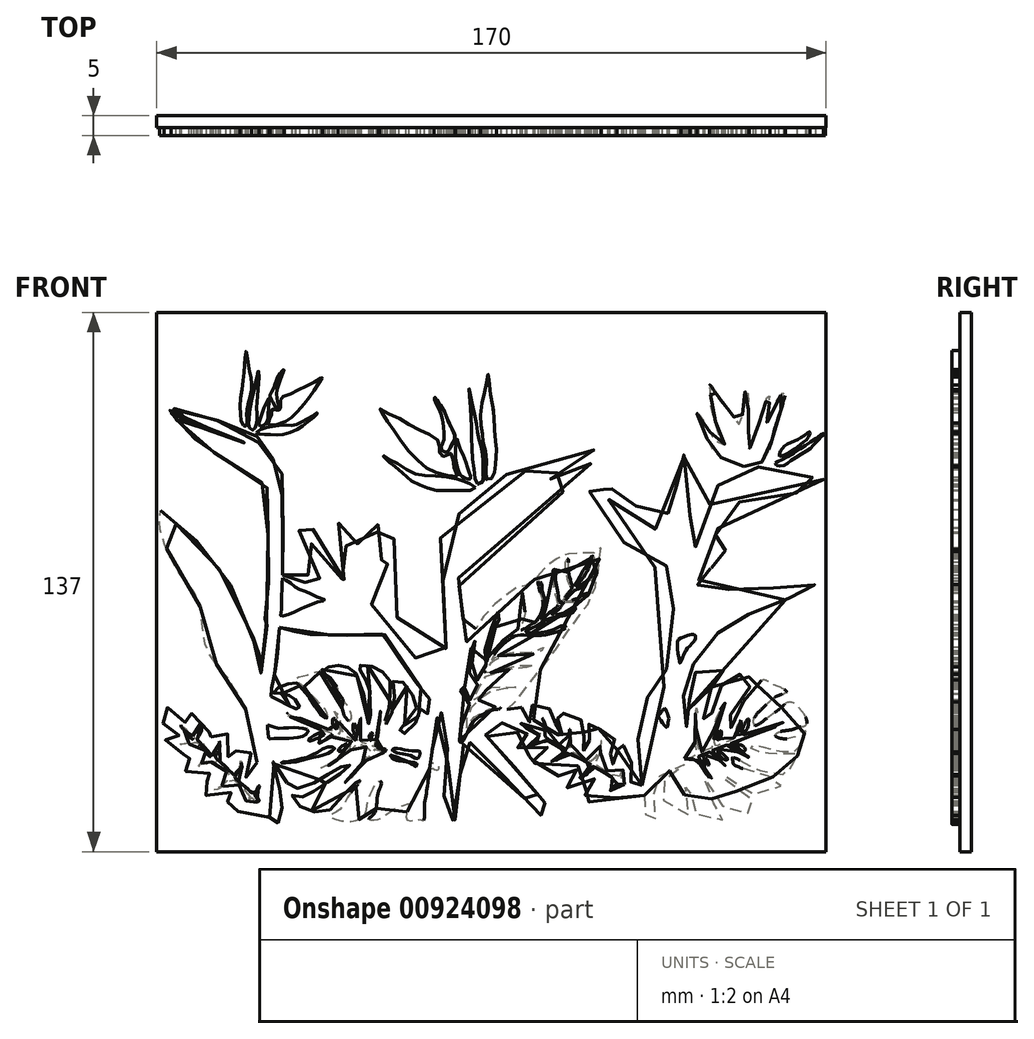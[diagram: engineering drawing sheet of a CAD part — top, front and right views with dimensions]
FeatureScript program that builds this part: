
annotation { "Feature Type Name" : "Feature", "Feature Type Description" : "" }
export const myFeature = defineFeature(function(context is Context, id is Id, definition is map)
    precondition{}
    {
        {
            var Q0;
            Q0=qCreatedBy(makeId("Front.planeOp"),FACE);
            var sketch = newSketch(context, id + "F0", { "sketchPlane" : qUnion([Q0])});
            skLineSegment(sketch, "E0.bottom", {"start": v(0, 0) * mm, "end": v(170, 0) * mm});
            skLineSegment(sketch, "E0.top", {"start": v(0, 137) * mm, "end": v(170, 137) * mm});
            skLineSegment(sketch, "E0.left", {"start": v(0, 0) * mm, "end": v(0, 137) * mm});
            skLineSegment(sketch, "E0.right", {"start": v(170, 0) * mm, "end": v(170, 137) * mm});
            skSolve(sketch);
        }
        {
            var Q0;
            Q0=makeQuery(id+"F0.imprint","IMPRINT",FACE,{"disambiguationData":[TD([[makeQuery(id+"F0.imprint","IMPRINT",EDGE,{"derivedFrom":sQuery(id+"F0.wireOp",EDGE,"E0.bottom")}),1.0]])]});
            extrude(context, id + "F1", {"entities" : qUnion([Q0]), "oppositeDirection" : true, "depth" : 3 * mm, "offsetDistance" : 25 * mm});
        }
        {
            var Q0;
            Q0=makeQuery(id+"F1.opExtrude","CAP_FACE",FACE,{"disambiguationData":[OSD([sQuery(id+"F0.wireOp",EDGE,"E0.bottom"),sQuery(id+"F0.wireOp",EDGE,"E0.top"),sQuery(id+"F0.wireOp",EDGE,"E0.left"),sQuery(id+"F0.wireOp",EDGE,"E0.right")])],"isStart":true});
            var sketch = newSketch(context, id + "F2", { "sketchPlane" : qUnion([Q0])});
            skFitSpline(sketch, "E1", {"points": [v(28.6, 8.72) * mm, v(25.87, 11.7) * mm, v(22.82, 10.25) * mm, v(21.68, 10.12) * mm, v(19.58, 10.31) * mm, v(17.93, 10.7) * mm, v(16.72, 11.26) * mm, v(16.15, 12.15) * mm, v(17.8, 12.66) * mm, v(19.27, 13.04) * mm, v(20.4, 13.74) * mm, v(20.54, 14.38) * mm, v(20.35, 15.27) * mm, v(19.4, 15.52) * mm, v(18.44, 14.57) * mm, v(16.85, 13.49) * mm, v(15.7, 12.98) * mm, v(14.12, 12.92) * mm, v(12.6, 14.25) * mm, v(11.38, 15.71) * mm, v(10.69, 16.35) * mm, v(9.99, 17.18) * mm, v(11.32, 17.68) * mm, v(12.97, 17.94) * mm, v(14.88, 18.7) * mm, v(15.52, 19.53) * mm, v(15.52, 20.42) * mm, v(14.44, 20.42) * mm, v(13.3, 19.9) * mm, v(12.21, 18.83) * mm, v(10.75, 18.38) * mm, v(8.65, 18.64) * mm, v(7.83, 19.72) * mm, v(6.1, 22.26) * mm, v(5.28, 23.34) * mm, v(4.84, 23.78) * mm, v(7.13, 23.91) * mm, v(8.72, 23.6) * mm, v(10.62, 23.6) * mm, v(10.88, 24.42) * mm, v(9.22, 24.87) * mm, v(7.38, 24.74) * mm, v(5.54, 24.61) * mm, v(4.71, 24.61) * mm, v(3.57, 25.82) * mm, v(2.61, 27.15) * mm, v(2.36, 28.1) * mm, v(1.6, 29.89) * mm, v(2.17, 30.14) * mm, v(3.19, 29.76) * mm, v(4.27, 29.5) * mm, v(5.35, 29.19) * mm, v(5.73, 29.82) * mm, v(5.6, 30.27) * mm, v(4.14, 30.52) * mm, v(2.93, 30.58) * mm, v(1.72, 31.28) * mm, v(1.66, 32.43) * mm, v(1.53, 33.76) * mm, v(1.72, 35.1) * mm, v(0.96, 36.62) * mm, v(0.96, 37.32) * mm, v(2.87, 36.56) * mm, v(4.14, 36.37) * mm, v(6.24, 36.11) * mm, v(7, 35.1) * mm, v(7.13, 33.57) * mm, v(7.44, 32.43) * mm, v(8.27, 31.92) * mm, v(8.65, 32.43) * mm, v(8.4, 33.57) * mm, v(8.08, 34.72) * mm, v(8.27, 35.1) * mm, v(9.73, 34.97) * mm, v(11.07, 34.33) * mm, v(12.27, 33.25) * mm, v(13.48, 32.05) * mm, v(13.3, 30.46) * mm, v(12.72, 29.25) * mm, v(12.6, 28.04) * mm, v(12.72, 27.09) * mm, v(13.35, 27.22) * mm, v(13.74, 28.61) * mm, v(13.93, 30.65) * mm, v(14.18, 31.8) * mm, v(15.52, 31.86) * mm, v(17.3, 30.71) * mm, v(18.12, 29.82) * mm, v(18.88, 29.38) * mm, v(19.77, 28.23) * mm, v(19.33, 26.64) * mm, v(18.31, 24.8) * mm, v(18, 23.78) * mm, v(17.49, 22.96) * mm, v(18.06, 22.64) * mm, v(19.14, 22.58) * mm, v(19.71, 24.23) * mm, v(20.1, 25.63) * mm, v(20.35, 26.96) * mm, v(20.47, 28.1) * mm, v(21.93, 27.09) * mm, v(23.4, 25.5) * mm, v(24.35, 24.67) * mm, v(24.8, 23.34) * mm, v(23.9, 21.37) * mm, v(23.02, 20.1) * mm, v(22.63, 19.08) * mm, v(23.14, 18.32) * mm, v(24.73, 18.38) * mm, v(24.99, 19.6) * mm, v(25.43, 21.12) * mm, v(25.43, 22.7) * mm], "startDerivative": vector(-157.55, 285.4) * mm, "endDerivative": vector(-16.17, 168.1) * mm});
            skFitSpline(sketch, "E2", {"points": [v(25.68, 23.09) * mm, v(25.43, 22.7) * mm, v(25.11, 24.61) * mm, v(24.48, 28.74) * mm, v(23.9, 31.67) * mm, v(23.33, 33.95) * mm, v(22.38, 36.81) * mm, v(20.73, 40) * mm, v(18.88, 42.66) * mm, v(17.68, 44.76) * mm, v(15.77, 46.73) * mm, v(15.13, 47.62) * mm, v(14.05, 49) * mm, v(12.34, 52.59) * mm, v(11.8, 56.1) * mm, v(11.18, 61.13) * mm, v(10.19, 64.9) * mm, v(6.41, 69.76) * mm, v(4.34, 72.9) * mm, v(2.82, 76.23) * mm, v(0.84, 81.44) * mm, v(0.75, 85.66) * mm, v(0.75, 86.83) * mm, v(2.64, 84.86) * mm, v(5.7, 82.88) * mm, v(8.12, 81.08) * mm, v(10.64, 78.47) * mm, v(13.33, 75.15) * mm, v(16.12, 71.37) * mm, v(19.35, 66.97) * mm, v(21.96, 61.94) * mm, v(24.12, 56.27) * mm, v(25.1, 50.8) * mm, v(25.65, 47.56) * mm, v(26.19, 44.95) * mm, v(26.28, 44.14) * mm, v(26.63, 46.84) * mm, v(27.17, 50.52) * mm, v(27.53, 54.48) * mm, v(27.9, 57.26) * mm, v(27.9, 57.8) * mm, v(26.72, 58.16) * mm, v(27.77, 58.36) * mm, v(27.8, 58.66) * mm, v(26.75, 58.7) * mm, v(26.37, 58.8) * mm, v(26.4, 59.11) * mm, v(27.4, 59.15) * mm, v(27.92, 59.19) * mm, v(27.92, 60.7) * mm, v(28, 62.1) * mm, v(28, 65.5) * mm, v(28.45, 68.92) * mm, v(28.27, 72.7) * mm, v(28.36, 75.13) * mm, v(28.3, 80.35) * mm, v(28.27, 85.28) * mm, v(28.36, 88.07) * mm, v(28.2, 90.79) * mm, v(28.11, 92.31) * mm, v(26.77, 93.7) * mm, v(24.7, 95.15) * mm, v(21.64, 96.8) * mm, v(19.76, 97.93) * mm, v(18.27, 98.83) * mm, v(13.76, 101.94) * mm, v(11.94, 103.11) * mm, v(9.75, 104.82) * mm, v(7.4, 107.28) * mm, v(6.12, 108.67) * mm, v(5, 109.8) * mm, v(3.71, 110.86) * mm, v(3.66, 111.45) * mm, v(4.46, 110.86) * mm, v(6.86, 109.69) * mm, v(9.38, 108.56) * mm, v(11.46, 107.76) * mm, v(13.22, 106.96) * mm, v(15.68, 106.1) * mm, v(18.67, 104.98) * mm, v(20.92, 104.45) * mm, v(22.79, 103.7) * mm, v(20.22, 105.04) * mm, v(16.96, 106.21) * mm, v(13.65, 107.44) * mm, v(10.28, 108.67) * mm, v(7.99, 109.63) * mm, v(4.3, 111.3) * mm, v(3.55, 111.89) * mm, v(3.08, 112.26) * mm, v(2.41, 112.64) * mm, v(1.8, 113.12) * mm, v(2.52, 113.63) * mm, v(3.7, 112.83) * mm, v(5.38, 112.32) * mm, v(6.53, 111.7) * mm, v(8.1, 111.01) * mm, v(9.81, 110.58) * mm, v(11.95, 110.18) * mm, v(14.7, 109.67) * mm, v(17.38, 109.25) * mm, v(21.25, 108.2) * mm, v(23.3, 107.06) * mm, v(25.15, 105.83) * mm, v(25.87, 104.68) * mm, v(25.95, 103.88) * mm, v(26.97, 103.05) * mm, v(27.74, 102.06) * mm, v(28.84, 100.86) * mm, v(29.5, 99.9) * mm, v(30.44, 98.61) * mm, v(31.36, 96.91) * mm, v(32.08, 94.66) * mm, v(31.9, 92.01) * mm, v(31.86, 89) * mm, v(32, 85.72) * mm, v(32.04, 82.35) * mm, v(31.95, 79.34) * mm, v(31.99, 77.09) * mm, v(31.9, 75) * mm, v(31.92, 73.08) * mm, v(31.92, 71.43) * mm, v(31.95, 70.35) * mm], "startDerivative": vector(-76, -164.8) * mm, "endDerivative": vector(7.76, -185.03) * mm});
            skFitSpline(sketch, "E3", {"points": [v(31.95, 69.57) * mm, v(31.88, 68.2) * mm, v(31.79, 65.88) * mm, v(31.7, 64.1) * mm, v(31.66, 61.08) * mm, v(31.47, 59.81) * mm, v(32.23, 59.94) * mm, v(34.01, 60.51) * mm, v(36.3, 61.6) * mm, v(37.6, 62.1) * mm, v(40.08, 63.12) * mm, v(41.8, 63.66) * mm, v(42.81, 63.98) * mm, v(40.84, 64.7) * mm, v(38.81, 65.66) * mm, v(36.68, 66.52) * mm, v(35.19, 67.25) * mm, v(33.8, 68.36) * mm, v(32.52, 69.19) * mm, v(31.95, 69.57) * mm]});
            skFitSpline(sketch, "E4", {"points": [v(31.15, 56.94) * mm, v(30.96, 54.94) * mm, v(30.84, 53.13) * mm, v(30.73, 51.16) * mm, v(30.54, 49.3) * mm, v(30.24, 47.46) * mm, v(29.94, 45.42) * mm, v(29.6, 43.3) * mm, v(29.22, 41.71) * mm, v(29.14, 40.47) * mm, v(29, 39.45) * mm, v(30.43, 38.73) * mm, v(31.98, 37.93) * mm, v(33.41, 37.18) * mm, v(34.92, 36.54) * mm, v(35.98, 36.08) * mm, v(36.36, 36.42) * mm, v(35.8, 37.44) * mm, v(35.23, 38.46) * mm, v(34.55, 39.33) * mm, v(33.6, 39.75) * mm, v(32.32, 40.09) * mm, v(30.96, 40.16) * mm, v(29.94, 40.16) * mm, v(29.6, 40.54) * mm, v(30.28, 41.26) * mm, v(31.86, 42.17) * mm, v(33.8, 42.7) * mm, v(35.26, 43.04) * mm, v(36.02, 42.4) * mm, v(37.46, 41) * mm, v(38.51, 39.56) * mm, v(39.53, 38) * mm, v(40.7, 36.27) * mm, v(41.58, 34.95) * mm, v(42.03, 34.46) * mm, v(42.97, 34.04) * mm, v(43.43, 33.97) * mm, v(43.35, 35.06) * mm, v(42.67, 36.3) * mm, v(41.58, 37.44) * mm, v(40.78, 38.35) * mm, v(39.38, 39.79) * mm, v(38.44, 40.84) * mm, v(37.3, 41.94) * mm, v(36.62, 42.4) * mm, v(35.76, 43.38) * mm, v(35.3, 43.8) * mm, v(35.9, 44.32) * mm, v(37.34, 44.74) * mm, v(39.04, 45.19) * mm, v(40.37, 45.68) * mm, v(41.5, 45.72) * mm, v(42.48, 44.25) * mm, v(43.7, 43.07) * mm, v(44.79, 41.64) * mm, v(45.54, 40.43) * mm, v(46.1, 39.37) * mm, v(46.53, 38.05) * mm, v(47.13, 36.35) * mm, v(47.62, 34.65) * mm, v(48.38, 33.59) * mm, v(48.87, 33.25) * mm, v(49.4, 33.78) * mm, v(49.44, 34.95) * mm, v(48.83, 36.42) * mm, v(47.85, 37.86) * mm, v(47.05, 39.1) * mm, v(46.56, 40.01) * mm, v(46.1, 41.07) * mm, v(45.4, 42.73) * mm, v(44.45, 43.83) * mm, v(43.2, 44.85) * mm, v(42.33, 45.5) * mm, v(41.8, 46.1) * mm, v(42.67, 46.63) * mm, v(44.33, 47.15) * mm, v(45.5, 47.27) * mm, v(46.68, 47.38) * mm, v(47.77, 47.08) * mm, v(49.17, 46.59) * mm, v(50.12, 46.1) * mm, v(50.83, 44.7) * mm, v(51.4, 43) * mm, v(51.93, 41.98) * mm, v(52.3, 40.8) * mm, v(52.8, 39) * mm, v(52.99, 37.44) * mm, v(53.21, 35.9) * mm, v(53.37, 34.3) * mm, v(53.48, 33.4) * mm, v(53.7, 32.72) * mm, v(53.82, 32.5) * mm, v(54.16, 32.98) * mm, v(54.35, 34.65) * mm, v(54.39, 36.16) * mm, v(54.2, 38.2) * mm, v(54.2, 39.97) * mm, v(53.93, 41.49) * mm, v(53.4, 42.92) * mm, v(52.84, 44.2) * mm, v(51.85, 45.9) * mm, v(51.25, 46.81) * mm, v(51.02, 47.34) * mm, v(51.74, 47.38) * mm, v(53.67, 47.27) * mm, v(55.14, 46.93) * mm, v(56.58, 46.1) * mm, v(57.98, 45.27) * mm, v(59.03, 43.83) * mm, v(59.41, 42.13) * mm, v(59.18, 39.22) * mm, v(59.03, 37.07) * mm, v(58.58, 34.68) * mm, v(57.98, 33.02) * mm, v(58.01, 32.53) * mm, v(58.35, 32.42) * mm, v(58.58, 33.21) * mm, v(59.56, 34.95) * mm, v(60.13, 36.84) * mm, v(60.36, 38.8) * mm, v(60.36, 41.79) * mm, v(60.1, 43.15) * mm, v(59.94, 43.87) * mm, v(61.57, 43.64) * mm, v(63.15, 42.56) * mm, v(64.45, 40.68) * mm, v(65.44, 39.01) * mm, v(65.8, 37.57) * mm, v(65.98, 36.18) * mm, v(64.72, 34.52) * mm, v(63.55, 33.3) * mm, v(62.79, 31.91) * mm, v(61.84, 31.06) * mm, v(61.57, 30.2) * mm, v(61.57, 29.76) * mm, v(62.65, 29.84) * mm, v(63.96, 30.97) * mm, v(65.48, 32.4) * mm, v(66.11, 33.53) * mm, v(66.74, 35.2) * mm, v(67.28, 36.72) * mm, v(68.5, 34.6) * mm, v(68.99, 36.45) * mm, v(69.21, 38.25) * mm, v(69.26, 38.83) * mm, v(66.97, 41.75) * mm, v(63.96, 45.7) * mm, v(59.2, 52.36) * mm, v(58.47, 53.48) * mm, v(58.43, 54.47) * mm, v(58.65, 54.74) * mm, v(57.53, 55.24) * mm, v(55.42, 55.33) * mm, v(52.5, 55.2) * mm, v(50.6, 55.06) * mm, v(47.5, 55.01) * mm, v(44.77, 55.01) * mm, v(41.58, 55.1) * mm, v(39.33, 55.2) * mm, v(36.81, 55.5) * mm, v(34.97, 56) * mm, v(32.59, 56.5) * mm, v(31.15, 56.94) * mm]});
            skFitSpline(sketch, "E5", {"points": [v(28.6, 8.72) * mm, v(29.2, 7.1) * mm, v(31.16, 7.63) * mm, v(31.77, 10.05) * mm, v(31.62, 14.38) * mm, v(30.71, 17.84) * mm, v(30.18, 20.4) * mm, v(29.88, 22.07) * mm, v(29.58, 22.83) * mm, v(30.56, 22.9) * mm, v(30.63, 21.62) * mm, v(31.84, 19.12) * mm, v(33.66, 16.78) * mm, v(34.72, 16.1) * mm, v(37.66, 16.63) * mm, v(40.69, 17.84) * mm, v(43.18, 19.42) * mm, v(45.45, 20.7) * mm, v(47.19, 21.84) * mm, v(48.47, 22.6) * mm, v(49, 21.92) * mm, v(48.32, 21.09) * mm, v(46.13, 19.5) * mm, v(43.94, 18.06) * mm, v(41.3, 16.17) * mm, v(39.33, 15.04) * mm, v(37.9, 14.2) * mm, v(36.3, 13.98) * mm, v(35.1, 14.36) * mm, v(34.34, 14.29) * mm, v(35.32, 12.7) * mm, v(37.2, 11.04) * mm, v(40, 10.2) * mm, v(42.42, 9.83) * mm, v(45.75, 12.32) * mm, v(48.1, 15.2) * mm, v(50.59, 17.61) * mm, v(52.02, 19.05) * mm, v(51.65, 17.84) * mm, v(49.68, 15.5) * mm, v(47.56, 12.17) * mm, v(46.5, 10.8) * mm, v(44.84, 9.68) * mm, v(43.86, 9.07) * mm, v(45.9, 8.09) * mm, v(48.62, 7.71) * mm, v(51.34, 8.16) * mm, v(52.85, 9.3) * mm, v(53.76, 13.38) * mm, v(55.2, 16.55) * mm, v(56.18, 17.99) * mm, v(57.01, 17.69) * mm, v(56.26, 15.2) * mm, v(55.88, 11.87) * mm, v(55.2, 9.6) * mm, v(54.22, 8.77) * mm, v(53.91, 8.24) * mm, v(56.1, 8.24) * mm, v(59.2, 10.13) * mm, v(61.47, 11.41) * mm, v(62.83, 11.8) * mm, v(64.04, 12.17) * mm, v(63.44, 8.24) * mm, v(66.91, 8.16) * mm, v(67.82, 7.94) * mm, v(67.97, 11.04) * mm, v(68.42, 14.59) * mm, v(68.95, 18.14) * mm, v(69.26, 20.48) * mm, v(69.4, 21.16) * mm, v(70.09, 21.16) * mm, v(71.45, 20.86) * mm, v(71.6, 21.84) * mm, v(70.31, 22.45) * mm, v(69.7, 22.67) * mm, v(69.78, 24.8) * mm, v(70.39, 29.48) * mm, v(70.84, 32.8) * mm, v(71.52, 35.52) * mm, v(71.52, 35.98) * mm, v(73.71, 34.01) * mm, v(74.7, 32.65) * mm, v(74.02, 30.61) * mm, v(73.56, 29.4) * mm, v(73.8, 26.3) * mm, v(74.02, 23.43) * mm, v(73.71, 19.88) * mm, v(73.1, 16.33) * mm, v(72.96, 13.23) * mm, v(72.5, 10.66) * mm, v(72.35, 9) * mm, v(72.5, 7.94) * mm, v(73.71, 8.16) * mm, v(75.68, 8.01) * mm, v(75.98, 9.22) * mm, v(76.2, 13.38) * mm, v(76.89, 17.69) * mm, v(77.2, 21.31) * mm, v(77.5, 24.04) * mm, v(77.87, 26.15) * mm, v(77.8, 27.2) * mm, v(79.3, 27.59) * mm, v(80.29, 28.12) * mm, v(81.95, 26.3) * mm, v(85.28, 22.75) * mm, v(88.45, 18.82) * mm, v(92.3, 14.9) * mm, v(94.65, 12.17) * mm, v(97.22, 9.68) * mm, v(98.73, 8.16) * mm, v(100.43, 7.92) * mm, v(102.51, 8.13) * mm, v(99.79, 11.23) * mm, v(96.96, 14.28) * mm, v(95.35, 16.47) * mm, v(92.84, 19.4) * mm, v(90.86, 21.54) * mm, v(89.37, 23.2) * mm, v(87.6, 25.12) * mm, v(84.88, 27.9) * mm, v(83.6, 29.61) * mm, v(82.8, 30.42) * mm, v(84.34, 31.7) * mm, v(86, 33.52) * mm, v(86.96, 34.26) * mm, v(87.5, 33.3) * mm, v(88.14, 31.97) * mm, v(88.78, 30.42) * mm, v(90.06, 30.1) * mm, v(91.67, 30.3) * mm, v(93.54, 30.47) * mm, v(94.07, 29.93) * mm, v(93.16, 29.13) * mm, v(92.04, 29.03) * mm, v(91.3, 29.24) * mm, v(90.33, 29.13) * mm, v(90.7, 28.17) * mm, v(91.61, 26.57) * mm, v(92.95, 25.4) * mm, v(94.5, 24.38) * mm, v(95.89, 24.16) * mm, v(97.01, 25.34) * mm, v(99.15, 26.51) * mm, v(100.22, 26.67) * mm, v(100.75, 25.98) * mm, v(99.36, 24.96) * mm, v(97.5, 24.16) * mm, v(96.16, 23.68) * mm, v(95.73, 22.93) * mm, v(96.42, 22.13) * mm, v(97.44, 21) * mm, v(98.61, 20.05) * mm, v(99.84, 19.57) * mm, v(101.18, 19.09) * mm, v(103.05, 19.89) * mm, v(104.33, 21.38) * mm, v(105.45, 22.45) * mm, v(106.26, 22.99) * mm, v(107, 21.76) * mm, v(106.63, 20.69) * mm, v(105.3, 19.83) * mm, v(103.64, 18.87) * mm, v(101.93, 18.28) * mm, v(102.57, 17.38) * mm, v(104.01, 16.36) * mm, v(105.94, 15.5) * mm, v(108.18, 15.08) * mm, v(109.36, 16.04) * mm, v(110.32, 17.32) * mm, v(110.96, 18.4) * mm, v(112.19, 18.66) * mm, v(113.1, 17.48) * mm, v(112.56, 16.2) * mm, v(110.64, 15.24) * mm, v(109.4, 14.81) * mm, v(108.77, 14.17) * mm, v(109.3, 13) * mm, v(111.01, 12.25) * mm, v(113.95, 12.25) * mm, v(115.66, 13.05) * mm, v(117.59, 14.44) * mm, v(118.81, 15.67) * mm, v(119.56, 16.15) * mm, v(121.43, 15.3) * mm, v(123.25, 14.38) * mm, v(123.84, 14.38) * mm], "startDerivative": vector(40.15, -413.53) * mm, "endDerivative": vector(178.1, 26.6) * mm});
            skFitSpline(sketch, "E6", {"points": [v(123.84, 14.38) * mm, v(123.84, 13.36) * mm, v(123.87, 12.2) * mm, v(123.99, 11.57) * mm, v(124.08, 10.17) * mm, v(124.12, 9.32) * mm, v(124.25, 7.71) * mm, v(124.67, 7.6) * mm, v(125.48, 7.88) * mm, v(126.24, 8.07) * mm, v(126.65, 8.37) * mm, v(126.58, 9.85) * mm, v(126.46, 11.47) * mm, v(126.46, 13.23) * mm, v(126.33, 14.9) * mm, v(126.24, 16.78) * mm, v(126.09, 18.12) * mm, v(126.09, 18.67) * mm, v(127.7, 19.2) * mm, v(129.73, 20.33) * mm, v(132.38, 21.46) * mm, v(134.04, 22.35) * mm, v(133.9, 21.77) * mm, v(132.6, 20.51) * mm, v(130.58, 19.2) * mm, v(129, 18.13) * mm, v(127.8, 16.96) * mm, v(127.2, 16.33) * mm, v(127.8, 14.76) * mm, v(128.96, 12.78) * mm, v(131.07, 11.43) * mm, v(133, 10.27) * mm, v(135.16, 9.37) * mm, v(134.94, 10.36) * mm, v(134.26, 12.56) * mm, v(134.17, 15.7) * mm, v(134.67, 17.32) * mm, v(135.07, 18.13) * mm, v(135.61, 17.6) * mm, v(135.57, 15.88) * mm, v(135.88, 13.9) * mm, v(135.93, 12.38) * mm, v(136.02, 11.03) * mm, v(136.1, 10.27) * mm, v(137.6, 9.37) * mm, v(139.52, 8.47) * mm, v(141.45, 7.93) * mm, v(143.7, 8.1) * mm, v(144.83, 8.24) * mm, v(145.18, 9.05) * mm, v(142.85, 10.8) * mm, v(140.92, 13.5) * mm, v(139.93, 15.48) * mm, v(139.25, 17.46) * mm, v(139.16, 18.49) * mm, v(140.02, 17) * mm, v(141.95, 13.95) * mm, v(143.61, 11.7) * mm, v(145.45, 9.73) * mm, v(147.57, 9.19) * mm, v(149.72, 9.68) * mm, v(152.38, 10.76) * mm, v(153.72, 12.15) * mm, v(152.87, 12.65) * mm, v(150.13, 13.5) * mm, v(146.76, 15.61) * mm, v(144.74, 17.82) * mm, v(143.2, 19.57) * mm, v(142.3, 20.56) * mm, v(142.67, 20.96) * mm, v(143.93, 19.75) * mm, v(145.63, 18.27) * mm, v(148.82, 16.06) * mm, v(151.52, 14.71) * mm, v(154, 13.77) * mm, v(156.55, 14.94) * mm, v(158.71, 16.92) * mm, v(159.61, 18.85) * mm, v(159.52, 19.25) * mm, v(157.36, 19.03) * mm, v(154.44, 19.34) * mm, v(152.55, 20.15) * mm, v(150.76, 20.74) * mm, v(148.78, 21.19) * mm, v(146.44, 22.4) * mm, v(146.3, 23.25) * mm, v(146.26, 23.88) * mm, v(148.38, 23.07) * mm, v(150.94, 21.68) * mm, v(153.68, 20.56) * mm, v(157.1, 19.97) * mm, v(159.84, 19.84) * mm, v(160.91, 21.28) * mm, v(161.9, 22.9) * mm, v(162.71, 24.7) * mm, v(161.45, 25) * mm, v(159.48, 24.78) * mm, v(156.87, 24.87) * mm, v(154.17, 25.14) * mm, v(151.84, 25.77) * mm, v(150.9, 26.3) * mm, v(150.8, 26.76) * mm, v(152.5, 27.07) * mm, v(154.53, 26.49) * mm, v(157.4, 25.73) * mm, v(159.3, 25.5) * mm, v(162.13, 25.46) * mm, v(163.25, 26.67) * mm, v(163.92, 28.15) * mm, v(164.55, 29.95) * mm, v(164.87, 31.07) * mm, v(163.74, 30.67) * mm, v(162.49, 29.45) * mm, v(160.91, 28.7) * mm, v(159.3, 28.7) * mm, v(157.81, 29) * mm, v(157.18, 29.5) * mm, v(157.77, 30.3) * mm, v(161.32, 31.03) * mm, v(163.12, 31.61) * mm, v(164.96, 32.24) * mm, v(164.82, 34.22) * mm, v(163.43, 36.29) * mm, v(162.08, 37.63) * mm, v(160.33, 37.95) * mm, v(158.67, 36.65) * mm, v(156.87, 35.3) * mm, v(154.8, 33.77) * mm, v(153.23, 32.6) * mm, v(151.97, 32.15) * mm, v(151.61, 33.27) * mm, v(152.42, 34.94) * mm, v(154.08, 36.65) * mm, v(155.84, 38.3) * mm, v(157.32, 39.43) * mm, v(159.39, 40.24) * mm, v(159.97, 40.78) * mm, v(157.32, 42.22) * mm, v(155.48, 43.16) * mm, v(154.13, 43.66) * mm, v(153.05, 42.98) * mm, v(151.34, 41.36) * mm, v(150, 39.61) * mm, v(148.65, 37.54) * mm, v(147.3, 34.8) * mm, v(146.4, 32.7) * mm, v(145.68, 31.3) * mm, v(145.18, 30.94) * mm, v(144.56, 31.39) * mm, v(144.42, 32.24) * mm, v(145.36, 34) * mm, v(146.8, 36.78) * mm, v(149.23, 40.02) * mm, v(150.76, 42) * mm, v(152.24, 43.48) * mm, v(151.57, 43.93) * mm, v(148.91, 45) * mm, v(147.48, 45.1) * mm, v(145.68, 45.1) * mm, v(145.05, 44.6) * mm, v(143.93, 43.07) * mm, v(142.94, 40.91) * mm, v(142.22, 38.9) * mm, v(141.54, 36.6) * mm, v(140.38, 33.5) * mm, v(139.7, 31.39) * mm, v(139.16, 31.7) * mm, v(138.9, 33.63) * mm, v(139.57, 36.2) * mm, v(140.24, 39.07) * mm, v(140.83, 41.45) * mm, v(141.5, 42.98) * mm, v(142, 44.33) * mm, v(143.16, 45.54) * mm, v(144.02, 46.17) * mm, v(143.44, 46.79) * mm, v(139.37, 46.6) * mm, v(136.96, 45.58) * mm, v(135.3, 44.37) * mm, v(135.3, 41.26) * mm, v(135.3, 38.78) * mm, v(135.18, 35.03) * mm, v(135.18, 31.91) * mm, v(134.73, 31.53) * mm, v(134.54, 32.49) * mm, v(134.48, 35.92) * mm, v(133.97, 38.46) * mm, v(133.72, 40.88) * mm, v(134.35, 43.54) * mm, v(135.96, 47) * mm, v(139.8, 52.35) * mm, v(142.05, 55.02) * mm, v(142.7, 55.88) * mm, v(143.22, 57.27) * mm, v(147.6, 59.3) * mm, v(154.98, 62.18) * mm, v(159.15, 63.79) * mm, v(163.21, 65.39) * mm, v(166.63, 66.78) * mm, v(167.38, 67.85) * mm, v(165.56, 67.2) * mm, v(160.54, 67.1) * mm, v(154.23, 66.89) * mm, v(148.68, 66.57) * mm, v(143.44, 66.57) * mm, v(139.06, 66.67) * mm, v(137.67, 67.53) * mm, v(137.37, 67.88) * mm, v(137.45, 68.57) * mm, v(138.13, 69.57) * mm, v(139.21, 70.47) * mm, v(140.6, 71.9) * mm, v(141.12, 72.29) * mm, v(141.87, 72.9) * mm, v(142.36, 73.37) * mm, v(142.76, 73.59) * mm, v(143.14, 73.94) * mm, v(143.57, 74.43) * mm, v(143.82, 74.72) * mm, v(143.93, 75.16) * mm, v(144.04, 75.6) * mm, v(144.04, 75.86) * mm, v(144.31, 76.1) * mm, v(144.42, 76.65) * mm, v(144.12, 76.6) * mm, v(143.45, 76.26) * mm, v(143.07, 76.51) * mm, v(142.61, 76.7) * mm, v(141.75, 76.86) * mm, v(140.88, 76.83) * mm, v(140.88, 77.88) * mm, v(141.3, 78.93) * mm, v(142.02, 80.86) * mm, v(142.82, 82.8) * mm, v(143.68, 84.36) * mm, v(144.38, 86.2) * mm, v(145.27, 87.76) * mm, v(146.22, 88.55) * mm, v(148.67, 88.87) * mm, v(151.34, 89.16) * mm, v(154.32, 89.54) * mm, v(158.4, 90.11) * mm, v(161.82, 90.94) * mm, v(164.62, 91.86) * mm, v(166.81, 92.56) * mm, v(169.26, 93.7) * mm, v(169.83, 94.47) * mm, v(168.75, 94.69) * mm, v(166.62, 95.07) * mm, v(163.47, 95.77) * mm, v(160.93, 96.3) * mm, v(157.82, 97.3) * mm, v(155.56, 97.67) * mm, v(151.86, 97.71) * mm, v(149.86, 97.33) * mm, v(148.68, 96.88) * mm, v(147.13, 95.94) * mm, v(145.47, 95.07) * mm, v(143.17, 93.56) * mm, v(142, 92.27) * mm, v(140.82, 88.95) * mm, v(138.74, 83.97) * mm, v(137.4, 79.27) * mm, v(136.33, 75.58) * mm, v(135.53, 73.6) * mm, v(135.2, 74.57) * mm, v(135.14, 81.45) * mm, v(135.4, 85.52) * mm, v(135.07, 89.52) * mm, v(134.63, 93.97) * mm, v(134.44, 96.83) * mm, v(134, 99.95) * mm, v(133.61, 102.49) * mm, v(133.17, 101.4) * mm, v(133.36, 98.04) * mm, v(132.85, 95.12) * mm, v(132.21, 92.83) * mm, v(132.09, 94.42) * mm, v(131.13, 97.09) * mm, v(130.62, 94.99) * mm, v(130.37, 91.56) * mm, v(129.86, 86.35) * mm, v(129.48, 82.91) * mm, v(128.72, 81) * mm, v(126.75, 81.9) * mm, v(123.57, 85.96) * mm, v(119.95, 89.78) * mm, v(117.09, 93.2) * mm, v(117.21, 91.56) * mm, v(118.23, 89.52) * mm, v(116.2, 91.62) * mm, v(113.72, 94.6) * mm, v(112.32, 97.09) * mm, v(111.05, 98.04) * mm, v(112.32, 94.86) * mm, v(113.72, 91.62) * mm, v(114.86, 89.27) * mm, v(112.83, 91.5) * mm, v(110.92, 92.7) * mm, v(109.4, 94.29) * mm, v(110.35, 90.48) * mm, v(111.56, 88.38) * mm, v(114.74, 84.25) * mm, v(116.39, 81.32) * mm, v(118.61, 78.66) * mm, v(120.4, 76.05) * mm, v(122.62, 73.25) * mm, v(124.33, 72.36) * mm, v(127.38, 72.36) * mm, v(129.67, 72.55) * mm, v(130.18, 70.84) * mm, v(131, 68.93) * mm, v(131.77, 67.02) * mm, v(132.68, 65.06) * mm, v(131.54, 62.34) * mm, v(130.71, 60.14) * mm, v(128.82, 57.05) * mm, v(128.6, 52.36) * mm, v(129.28, 47.9) * mm, v(129.65, 44.5) * mm, v(129.58, 42.76) * mm, v(127.84, 40.65) * mm, v(126.25, 38.3) * mm, v(125.5, 37.77) * mm, v(124.74, 39.06) * mm, v(123.84, 40.12) * mm, v(123.76, 38.9) * mm, v(123.38, 35.8) * mm, v(123.15, 32.18) * mm, v(122.25, 29.3) * mm, v(122.55, 27.2) * mm, v(122.85, 25.08) * mm, v(122.78, 22.28) * mm, v(123, 19.48) * mm, v(123.08, 18.05) * mm, v(123.23, 16.84) * mm], "startDerivative": vector(0.15, -464.66) * mm, "endDerivative": vector(79.05, -529.4) * mm});
            skFitSpline(sketch, "E7", {"points": [v(123.23, 16.84) * mm, v(122.45, 16.84) * mm, v(121.47, 17.14) * mm, v(120.89, 17.46) * mm, v(120.43, 17.72) * mm, v(120.6, 18.63) * mm, v(120.98, 21.48) * mm, v(120.26, 23.3) * mm, v(119.6, 25.02) * mm, v(118.62, 26.98) * mm, v(117.64, 27.74) * mm, v(117.15, 27.81) * mm, v(117.07, 26.68) * mm, v(117.13, 25.45) * mm, v(117, 23.6) * mm, v(116.31, 22.58) * mm, v(115.44, 22.22) * mm, v(114.69, 22.71) * mm, v(114.69, 23.6) * mm, v(115.31, 24.98) * mm, v(115.9, 26.26) * mm, v(116.3, 27.64) * mm, v(116.33, 28.59) * mm, v(115.37, 29.38) * mm, v(113.74, 30.46) * mm, v(112.72, 31) * mm, v(111.93, 31.57) * mm, v(111.02, 32.1) * mm, v(109.93, 32.54) * mm, v(109.68, 31.76) * mm, v(109.81, 30.36) * mm, v(109.87, 28.8) * mm, v(109.8, 27.4) * mm, v(109.34, 26.4) * mm, v(108.95, 25.77) * mm, v(108.38, 25.77) * mm, v(107.85, 26.3) * mm, v(107.72, 27.3) * mm, v(108.47, 28.98) * mm, v(108.87, 30.33) * mm, v(109.08, 31.65) * mm, v(107.55, 33.67) * mm, v(106.22, 34.01) * mm, v(103.8, 35.05) * mm, v(102.62, 35.43) * mm, v(101.58, 35.75) * mm, v(101.52, 34.75) * mm, v(102.07, 33.25) * mm, v(102.7, 31.74) * mm, v(102.92, 30.17) * mm, v(102.94, 29.51) * mm, v(102.2, 29.59) * mm, v(101.58, 31.06) * mm, v(101.22, 33.75) * mm, v(101.03, 35.14) * mm, v(100.31, 36.1) * mm, v(98.76, 36.58) * mm, v(96.7, 37.1) * mm, v(95.74, 37.24) * mm, v(94.4, 37.35) * mm, v(93.85, 37.01) * mm, v(94.45, 35.98) * mm, v(95.5, 34.5) * mm, v(95.72, 33.5) * mm, v(95.51, 32.8) * mm, v(94.66, 33) * mm, v(94.07, 34.31) * mm, v(93.3, 36.01) * mm, v(92.32, 36.8) * mm, v(90.79, 36.7) * mm, v(89.4, 36.18) * mm, v(88.95, 36.15) * mm, v(90.22, 37.17) * mm, v(94.14, 42.1) * mm, v(99.28, 48.62) * mm, v(102.9, 53.65) * mm, v(107.24, 59.99) * mm, v(109.15, 62.3) * mm, v(111.44, 67.47) * mm, v(112.07, 70.69) * mm, v(112.45, 74.37) * mm, v(112.65, 76.17) * mm, v(112.8, 77.31) * mm, v(111.66, 76.17) * mm, v(109.82, 75.76) * mm, v(107.01, 75.97) * mm, v(103.98, 75.52) * mm, v(101.42, 74.4) * mm, v(98.47, 72.01) * mm, v(96.43, 69.67) * mm, v(94.65, 68.03) * mm, v(93.01, 67.34) * mm, v(91.2, 66.93) * mm, v(89.37, 65.63) * mm, v(86.88, 63.79) * mm, v(83.76, 60.69) * mm, v(81.49, 57.36) * mm, v(80.16, 55.27) * mm, v(78.32, 52.75) * mm, v(77.37, 51.18) * mm, v(77.33, 53.2) * mm, v(77.46, 57.85) * mm, v(77.85, 59.42) * mm, v(78.53, 61.82) * mm, v(79.18, 63.64) * mm, v(78.23, 63.86) * mm, v(77.08, 63.96) * mm, v(76.55, 64.28) * mm, v(76.74, 67.47) * mm, v(76.87, 72.6) * mm, v(79.92, 75.5) * mm, v(85.64, 79.05) * mm, v(94.79, 84.93) * mm, v(100.45, 89.15) * mm, v(105.28, 93.41) * mm, v(109.06, 97.42) * mm, v(111.76, 100.12) * mm, v(110.58, 99.39) * mm, v(107.28, 97.7) * mm, v(103.2, 95.92) * mm, v(100.06, 94.46) * mm, v(101.05, 95.86) * mm, v(106.3, 98.15) * mm, v(110.68, 100.25) * mm, v(112.84, 101.8) * mm, v(112.23, 102.4) * mm, v(106.2, 99.39) * mm, v(99.9, 97.7) * mm, v(92.4, 96.5) * mm, v(87.16, 95.38) * mm, v(82.8, 93.2) * mm, v(80.33, 91.32) * mm, v(79.66, 89.44) * mm, v(78.55, 87.82) * mm, v(74.58, 83.34) * mm, v(72.23, 80.07) * mm, v(70.96, 76.03) * mm, v(70.9, 73.36) * mm, v(73.52, 66.77) * mm, v(73.58, 63.21) * mm, v(74.03, 58.44) * mm, v(74.28, 54.85) * mm, v(73.7, 52.4) * mm, v(72.44, 48.45) * mm, v(71.28, 44.45) * mm, v(70.78, 42.7) * mm, v(68.17, 45.8) * mm, v(64.53, 50.84) * mm, v(62.92, 53.9) * mm, v(62.2, 57.98) * mm, v(57.88, 61.67) * mm, v(53.61, 63.06) * mm, v(50.74, 64.1) * mm, v(50.33, 65.17) * mm, v(53.61, 66.92) * mm, v(57.2, 70.52) * mm, v(59.73, 76.72) * mm, v(60.62, 81.26) * mm, v(60.17, 79.96) * mm, v(58.92, 77.93) * mm, v(58.02, 75.55) * mm, v(55.77, 72.63) * mm, v(53.93, 71.15) * mm, v(54.6, 72.54) * mm, v(56.04, 76.94) * mm, v(56.12, 82.11) * mm, v(56.31, 85.06) * mm, v(56.23, 86.99) * mm, v(55.18, 85.6) * mm, v(53.48, 82.83) * mm, v(51.89, 79.96) * mm, v(50.8, 77.96) * mm, v(49.85, 76.4) * mm, v(49.58, 75.54) * mm, v(48.53, 76.67) * mm, v(47.5, 80) * mm, v(46.4, 84.42) * mm, v(46.18, 83.51) * mm, v(46.07, 80.15) * mm, v(46.52, 76.37) * mm, v(47.05, 74.78) * mm, v(47.05, 73.88) * mm, v(47.35, 70.85) * mm, v(47.47, 68.78) * mm, v(45.54, 72.18) * mm, v(43.16, 76.4) * mm, v(40.82, 81.06) * mm, v(39.72, 82.34) * mm, v(39.99, 81.1) * mm, v(40.9, 78.64) * mm, v(42.18, 75.16) * mm, v(42.1, 74.9) * mm, v(38.44, 79.28) * mm, v(35.98, 81.85) * mm, v(35.45, 82.23) * mm, v(36.06, 80.26) * mm, v(37.68, 76.9) * mm, v(39.34, 73.35) * mm, v(40.7, 70.32) * mm, v(41.84, 68.78) * mm, v(40.33, 69.34) * mm, v(37.68, 70.55) * mm, v(35.45, 70.93) * mm, v(34.47, 71.2) * mm, v(36.02, 69.5) * mm, v(39.5, 67.72) * mm, v(41.8, 66.81) * mm, v(41.53, 66.55) * mm, v(37.6, 68.06) * mm, v(34.66, 69.34) * mm, v(31.95, 70.35) * mm], "startDerivative": vector(-273.48, -21.12) * mm, "endDerivative": vector(-531.95, 194.07) * mm});
            skArc(sketch, "E8", {"start": v(9.72, 28.63) * mm, "mid": v(10.86, 30.48) * mm, "end": v(10.8, 32.65) * mm});
            skSolve(sketch);
        }
        {
            var Q0;
            Q0 = qSketchRegion(id + "F2", true);
            extrude(context, id + "F3", {"entities" : qUnion([Q0]), "operationType" : NewBodyOperationType.ADD, "depth" : 2 * mm, "offsetDistance" : 25 * mm});
        }
        {
            var Q0;
            {var subQ0=sQuery(id+"F0.wireOp",EDGE,"E0.left");var subQ1=sQuery(id+"F0.wireOp",EDGE,"E0.top");var subQ2=sQuery(id+"F0.wireOp",EDGE,"E0.right");var subQ3=sQuery(id+"F0.wireOp",EDGE,"E0.bottom");Q0=makeQuery(id+"F3.boolean.opBoolean","SPLIT",FACE,{"disambiguationData":[TD([makeQuery(id+"F1.opExtrude","SWEPT_FACE",FACE,{"disambiguationData":[OSD([subQ3])]})])],"derivedFrom":makeQuery(id+"F1.opExtrude","CAP_FACE",FACE,{"disambiguationData":[OSD([subQ3,subQ1,subQ0,subQ2])],"isStart":true})});}
            var sketch = newSketch(context, id + "F4", { "sketchPlane" : qUnion([Q0])});
            skFitSpline(sketch, "E9", {"points": [v(22.05, 108.28) * mm, v(21.36, 110.1) * mm, v(21.16, 113.37) * mm, v(21.73, 118.05) * mm, v(22.17, 122.24) * mm, v(22.46, 125.66) * mm, v(22.7, 127.3) * mm, v(22.82, 126.89) * mm, v(23.2, 124.48) * mm, v(23.6, 121.96) * mm, v(24.09, 119.68) * mm, v(24, 117.03) * mm, v(23.35, 114.22) * mm, v(22.87, 110.76) * mm, v(22.95, 108.44) * mm, v(22.05, 108.28) * mm]});
            skFitSpline(sketch, "E10", {"points": [v(24.37, 107.1) * mm, v(23.48, 107.91) * mm, v(23.44, 109.46) * mm, v(23.72, 112.55) * mm, v(24.2, 115.36) * mm, v(24.94, 118.5) * mm, v(25.47, 120.9) * mm, v(25.8, 122.33) * mm, v(25.92, 120.41) * mm, v(25.76, 117.36) * mm, v(25.43, 114.18) * mm, v(25.43, 111.66) * mm, v(25.43, 109.42) * mm, v(24.98, 107.75) * mm, v(24.37, 107.1) * mm]});
            skFitSpline(sketch, "E11", {"points": [v(25.92, 108.44) * mm, v(26.4, 110.4) * mm, v(27.1, 112.51) * mm, v(28.12, 114.63) * mm, v(28.36, 115.12) * mm, v(28.53, 113.82) * mm, v(28.28, 111.5) * mm, v(28.32, 110.64) * mm, v(27.63, 108.77) * mm, v(26.49, 108.2) * mm, v(25.92, 108.44) * mm]});
            skFitSpline(sketch, "E12", {"points": [v(30.36, 112.84) * mm, v(29.58, 114.1) * mm, v(29.1, 114.91) * mm, v(28.73, 115.93) * mm, v(29.5, 117.44) * mm, v(30.6, 120.2) * mm, v(32.23, 122.53) * mm, v(32.07, 121.63) * mm, v(31.1, 119.1) * mm, v(30.44, 116.22) * mm, v(30.8, 114.14) * mm, v(30.97, 113.08) * mm, v(30.36, 112.84) * mm]});
            skFitSpline(sketch, "E13", {"points": [v(28.28, 108.44) * mm, v(32.35, 109.1) * mm, v(34.84, 110.92) * mm, v(37.93, 114.34) * mm, v(39.97, 117.32) * mm, v(41.76, 119.92) * mm, v(42.13, 120.66) * mm, v(40.99, 119.8) * mm, v(37.24, 118) * mm, v(33.74, 116.22) * mm, v(31.54, 115.2) * mm, v(31.5, 114.14) * mm, v(31.38, 112.84) * mm, v(31.13, 112.27) * mm, v(30.32, 112.27) * mm, v(29.3, 112.39) * mm, v(29.18, 111.53) * mm, v(28.9, 110.52) * mm, v(28.28, 108.44) * mm]});
            skFitSpline(sketch, "E14", {"points": [v(25.29, 106.55) * mm, v(27.13, 107.54) * mm, v(29.23, 108.03) * mm, v(32.5, 108.46) * mm, v(34.56, 108.34) * mm, v(36.3, 109) * mm, v(38.5, 110.08) * mm, v(40.5, 111.37) * mm, v(40.8, 111.6) * mm, v(40.66, 111.1) * mm, v(38.55, 109.38) * mm, v(36.2, 107.59) * mm, v(32.98, 106.2) * mm, v(30.18, 105.94) * mm, v(27.73, 106.06) * mm, v(25.77, 106.2) * mm, v(25.29, 106.55) * mm]});
            skFitSpline(sketch, "E15", {"points": [v(80.94, 92.56) * mm, v(79.77, 91.89) * mm, v(74.93, 91.89) * mm, v(70.62, 91.84) * mm, v(67.77, 92.9) * mm, v(65.15, 93.92) * mm, v(61.28, 97.26) * mm, v(59.63, 98.52) * mm, v(58.08, 99.92) * mm, v(57.35, 100.9) * mm, v(58.56, 99.97) * mm, v(60.55, 98.96) * mm, v(64.13, 96.68) * mm, v(67.43, 95.61) * mm, v(71.78, 95.42) * mm, v(76.05, 94.7) * mm, v(77.7, 94.21) * mm, v(79.24, 93.58) * mm, v(80.94, 92.56) * mm]});
            skFitSpline(sketch, "E16", {"points": [v(76.43, 95.34) * mm, v(73.28, 95.77) * mm, v(69.85, 96.7) * mm, v(67.13, 98.68) * mm, v(63.89, 101.83) * mm, v(61.03, 105.9) * mm, v(58.9, 108.94) * mm, v(57.45, 111.12) * mm, v(56.58, 112.58) * mm, v(58.08, 111.6) * mm, v(61.61, 110.15) * mm, v(64.52, 108.31) * mm, v(68.15, 106.57) * mm, v(70.81, 105.07) * mm, v(71.88, 103.81) * mm, v(71.69, 102.5) * mm, v(71.88, 101.34) * mm, v(72.22, 100.47) * mm, v(74.1, 100.95) * mm, v(74.88, 101.15) * mm, v(75.27, 99.7) * mm, v(75.42, 97.85) * mm, v(76.43, 95.34) * mm]});
            skFitSpline(sketch, "E17", {"points": [v(77.06, 95.82) * mm, v(78.03, 95.05) * mm, v(79.63, 94.7) * mm, v(79.24, 96.74) * mm, v(77.98, 100.37) * mm, v(76.87, 102.94) * mm, v(76.19, 104.92) * mm, v(75.95, 102.5) * mm, v(75.95, 99.4) * mm, v(77.06, 95.82) * mm]});
            skFitSpline(sketch, "E18", {"points": [v(73.48, 101.44) * mm, v(74.88, 103.28) * mm, v(75.8, 105.22) * mm, v(74.45, 108.46) * mm, v(73.24, 111.46) * mm, v(71.44, 114.42) * mm, v(70.52, 115.48) * mm, v(70.81, 114.03) * mm, v(71.93, 111.9) * mm, v(72.7, 109) * mm, v(73, 105.07) * mm, v(72.46, 103.42) * mm, v(72.17, 102.3) * mm, v(73.48, 101.44) * mm]});
            skFitSpline(sketch, "E19", {"points": [v(81.48, 93.5) * mm, v(80.68, 95.97) * mm, v(80.1, 101.62) * mm, v(79.99, 108.01) * mm, v(79.64, 113.2) * mm, v(79.35, 117.68) * mm, v(79.93, 114.92) * mm, v(81.2, 108.82) * mm, v(81.71, 105.3) * mm, v(82.46, 102.6) * mm, v(82.87, 99.2) * mm, v(82.87, 95.92) * mm, v(82.92, 94.3) * mm, v(81.48, 93.5) * mm]});
            skFitSpline(sketch, "E20", {"points": [v(83.73, 94.65) * mm, v(83.73, 97.64) * mm, v(83.62, 101.39) * mm, v(82.87, 104.38) * mm, v(82.64, 106.8) * mm, v(82.23, 110.37) * mm, v(82.93, 115.68) * mm, v(83.8, 119.07) * mm, v(84.2, 121.4) * mm, v(84.68, 116.75) * mm, v(85.55, 112.1) * mm, v(85.84, 105.8) * mm, v(86.29, 102.63) * mm, v(86.2, 100.48) * mm, v(86, 98.28) * mm, v(85.64, 95.75) * mm, v(84.82, 94.61) * mm, v(83.73, 94.65) * mm]});
            skFitSpline(sketch, "E21", {"points": [v(149.13, 97.94) * mm, v(145.91, 98.97) * mm, v(143.17, 100.27) * mm, v(141.26, 102.39) * mm, v(139.68, 105.06) * mm, v(138.58, 108.07) * mm, v(137.28, 111.57) * mm, v(139.13, 109.1) * mm, v(140.91, 106.02) * mm, v(142.49, 104.17) * mm, v(144.2, 103.55) * mm, v(143.1, 105.6) * mm, v(141.94, 109.1) * mm, v(140.78, 113.48) * mm, v(140.64, 116.98) * mm, v(140.5, 118.62) * mm, v(141.53, 117.25) * mm, v(144.2, 113.55) * mm, v(146.94, 109.92) * mm, v(147.7, 108.55) * mm, v(148.58, 110.06) * mm, v(149.06, 113) * mm, v(149.34, 115.81) * mm, v(149.68, 117.39) * mm, v(150.43, 114.85) * mm, v(150.16, 110.95) * mm, v(150.36, 108.14) * mm, v(150.36, 106.36) * mm, v(150.36, 103.62) * mm, v(150.5, 102.32) * mm, v(151.46, 104.65) * mm, v(152.7, 108.21) * mm, v(153.92, 111.7) * mm, v(154.6, 113.96) * mm, v(154.95, 115.4) * mm, v(155.36, 116.43) * mm, v(155.7, 114.1) * mm, v(154.81, 111.09) * mm, v(154.81, 108.96) * mm, v(156.8, 113.35) * mm, v(159, 116.43) * mm, v(159.68, 117.04) * mm, v(158.38, 111.7) * mm, v(156.66, 106.36) * mm, v(155.64, 102.6) * mm, v(154.2, 99.65) * mm, v(153.3, 98.62) * mm, v(151.46, 98.55) * mm, v(149.13, 97.94) * mm]});
            skFitSpline(sketch, "E22", {"points": [v(158.2, 100.44) * mm, v(158.44, 101.7) * mm, v(159.75, 103.3) * mm, v(162.12, 104.42) * mm, v(164.4, 105.72) * mm, v(165.9, 106.7) * mm, v(165.46, 105.2) * mm, v(163.58, 103.54) * mm, v(161.25, 101.8) * mm, v(158.2, 100.44) * mm]});
            skFitSpline(sketch, "E23", {"points": [v(157.23, 98.8) * mm, v(157.62, 98.07) * mm, v(159.31, 98.22) * mm, v(161.35, 99.52) * mm, v(165.27, 101.95) * mm, v(167.26, 103.69) * mm, v(169.34, 106.3) * mm, v(167.5, 105.1) * mm, v(163.24, 102.24) * mm, v(158.64, 99.52) * mm, v(157.23, 98.8) * mm]});
            skSolve(sketch);
        }
        {
            var Q0;
            Q0 = qSketchRegion(id + "F4", true);
            extrude(context, id + "F5", {"entities" : qUnion([Q0]), "operationType" : NewBodyOperationType.ADD, "depth" : 2 * mm, "offsetDistance" : 25 * mm});
        }
        {
            var Q0;
            Q0=makeQuery(id+"F3.opExtrude","CAP_FACE",FACE,{"disambiguationData":[OSD([sQuery(id+"F2.wireOp",EDGE,"E1"),sQuery(id+"F2.wireOp",EDGE,"E2"),sQuery(id+"F2.wireOp",EDGE,"E3"),sQuery(id+"F2.wireOp",EDGE,"E4"),sQuery(id+"F2.wireOp",EDGE,"E5"),sQuery(id+"F2.wireOp",EDGE,"E6"),sQuery(id+"F2.wireOp",EDGE,"E7")])],"isStart":false});
            var sketch = newSketch(context, id + "F6", { "sketchPlane" : qUnion([Q0])});
            skFitSpline(sketch, "E24", {"points": [v(25.46, 12.51) * mm, v(24.3, 13.66) * mm, v(23.64, 13.18) * mm, v(22.98, 12.82) * mm, v(22.43, 12.82) * mm, v(23.46, 13.48) * mm, v(23.7, 14.2) * mm, v(21.89, 16.02) * mm, v(20.62, 17.35) * mm, v(19.43, 18.31) * mm, v(18.56, 17.96) * mm, v(17.3, 16.87) * mm, v(15.72, 15.96) * mm, v(14.27, 15.6) * mm, v(15.96, 16.39) * mm, v(17.6, 17.66) * mm, v(18.56, 18.87) * mm, v(18.62, 19.53) * mm, v(17.84, 20.38) * mm, v(16.38, 21.47) * mm, v(15.3, 22.68) * mm, v(14.58, 23.06) * mm, v(13.12, 22.5) * mm, v(11.85, 22.07) * mm, v(10.4, 21.65) * mm, v(10.94, 22.17) * mm, v(13.12, 23.22) * mm, v(13.96, 23.77) * mm, v(13.06, 24.55) * mm, v(12.21, 26) * mm, v(10.94, 27.15) * mm, v(10.1, 27.7) * mm, v(8.76, 27.4) * mm, v(7.61, 27.15) * mm, v(5.86, 27.27) * mm, v(6.64, 27.46) * mm, v(8.34, 27.82) * mm, v(9.37, 28.24) * mm, v(8.22, 29.27) * mm, v(7.25, 30.6) * mm, v(6.28, 31.63) * mm, v(6.16, 32.17) * mm, v(7.85, 30.6) * mm, v(9.25, 29.27) * mm, v(9.88, 28.77) * mm, v(10.64, 30.06) * mm, v(11, 31.5) * mm, v(11.06, 32.78) * mm, v(11.36, 30.84) * mm, v(10.58, 29.27) * mm, v(10.43, 28.3) * mm, v(11.9, 27.21) * mm, v(12.82, 25.88) * mm, v(13.96, 24.55) * mm, v(14.7, 24.8) * mm, v(15.23, 26.25) * mm, v(15.78, 28.18) * mm, v(16.02, 26.8) * mm, v(15.42, 25.04) * mm, v(14.93, 24.07) * mm, v(16.02, 22.86) * mm, v(17.41, 21.77) * mm, v(18.44, 20.56) * mm, v(19.47, 19.4) * mm, v(20.07, 20.32) * mm, v(21.22, 22.2) * mm, v(21.28, 23.1) * mm, v(21.59, 21.16) * mm, v(20.2, 19.65) * mm, v(19.86, 18.77) * mm, v(20.47, 18.14) * mm, v(21.08, 17.63) * mm, v(21.84, 17.07) * mm, v(22.86, 16.28) * mm, v(23.8, 15.24) * mm, v(24.74, 14.98) * mm, v(25.43, 15.77) * mm, v(26, 16.97) * mm, v(26.04, 16.38) * mm, v(25.25, 14.9) * mm, v(24.9, 14.4) * mm, v(25.48, 13.69) * mm, v(26.07, 13.15) * mm, v(25.46, 12.51) * mm]});
            skFitSpline(sketch, "E25", {"points": [v(28.15, 32.21) * mm, v(28.3, 30.33) * mm, v(28.5, 28.7) * mm, v(30.13, 28.8) * mm, v(32.88, 28.75) * mm, v(35.58, 29.06) * mm, v(37.76, 29.62) * mm, v(38.48, 30.74) * mm, v(37.3, 31.35) * mm, v(34.97, 31.55) * mm, v(31.86, 31.4) * mm, v(29.73, 31.65) * mm, v(28.15, 32.21) * mm]});
            skFitSpline(sketch, "E26", {"points": [v(41.88, 30.4) * mm, v(40.66, 29.98) * mm, v(39.56, 29.3) * mm, v(38.67, 28.67) * mm, v(38.63, 28.23) * mm, v(39.4, 28.31) * mm, v(40.29, 28.62) * mm, v(41.23, 29.02) * mm, v(41.98, 29.4) * mm, v(42.45, 29.7) * mm, v(42.53, 29.99) * mm, v(42.2, 30.22) * mm, v(41.88, 30.4) * mm]});
            skFitSpline(sketch, "E27", {"points": [v(32.25, 22.93) * mm, v(31.67, 22.6) * mm, v(33.25, 22.69) * mm, v(35.54, 22.9) * mm, v(38.2, 23.62) * mm, v(40.99, 24.2) * mm, v(42.99, 24.83) * mm, v(44.62, 25.65) * mm, v(45.16, 26.35) * mm, v(44.38, 26.7) * mm, v(42.23, 26.1) * mm, v(39.48, 24.56) * mm, v(37.12, 23.74) * mm, v(34.67, 23.17) * mm, v(32.76, 22.87) * mm, v(32.25, 22.93) * mm]});
            skFitSpline(sketch, "E28", {"points": [v(48.3, 27.4) * mm, v(46.96, 26.76) * mm, v(46.27, 26.1) * mm, v(46.14, 25.56) * mm, v(46.7, 25.51) * mm, v(47.97, 26.38) * mm, v(48.28, 26.84) * mm, v(48.3, 27.4) * mm]});
            skFitSpline(sketch, "E29", {"points": [v(65.84, 21.66) * mm, v(66.05, 22.32) * mm, v(64.47, 22.77) * mm, v(61.78, 23.74) * mm, v(60, 24.4) * mm, v(59.33, 24.5) * mm, v(60.15, 23.54) * mm, v(61.52, 23.13) * mm, v(63.35, 22.88) * mm, v(65.08, 22.16) * mm, v(65.84, 21.66) * mm]});
            skFitSpline(sketch, "E30", {"points": [v(66.3, 23.69) * mm, v(66.86, 25.37) * mm, v(66.15, 25.57) * mm, v(63.4, 25.78) * mm, v(60.45, 26.23) * mm, v(59.8, 25.83) * mm, v(61.06, 25.16) * mm, v(63.1, 24.76) * mm, v(64.73, 24.35) * mm, v(66.3, 23.69) * mm]});
            skFitSpline(sketch, "E31", {"points": [v(57.69, 25.18) * mm, v(56.69, 25.6) * mm, v(55.2, 25.97) * mm, v(54.33, 24.97) * mm, v(53, 22.86) * mm, v(51.7, 21.31) * mm, v(50.28, 19.68) * mm, v(47.76, 17.58) * mm, v(47.88, 18.01) * mm, v(49.54, 19.44) * mm, v(51.6, 21.73) * mm, v(53.12, 23.92) * mm, v(54.01, 25.24) * mm, v(54.44, 26.05) * mm, v(54, 26.32) * mm, v(53, 26.77) * mm, v(52.02, 27.06) * mm, v(51, 27.47) * mm, v(50.61, 27.58) * mm, v(49.91, 26.65) * mm, v(48.9, 25.4) * mm, v(47.25, 24.02) * mm, v(45.43, 22.89) * mm, v(43.26, 21.76) * mm, v(41.46, 21.22) * mm, v(42.92, 21.97) * mm, v(45.3, 23.14) * mm, v(48.33, 25.23) * mm, v(49.25, 26.47) * mm, v(50.04, 27.7) * mm, v(49.01, 28.18) * mm, v(47.47, 28.8) * mm, v(46.1, 29.25) * mm, v(45.27, 29.65) * mm, v(44.01, 29) * mm, v(42.8, 28.18) * mm, v(41.3, 27.26) * mm, v(40.5, 27) * mm, v(41.08, 27.44) * mm, v(42.22, 28.09) * mm, v(44.33, 29.64) * mm, v(44.55, 29.9) * mm, v(40.71, 31.35) * mm, v(37.99, 32.6) * mm, v(35.45, 33.65) * mm, v(33.06, 34.74) * mm, v(32.54, 35.4) * mm, v(33.72, 34.83) * mm, v(35.36, 34.16) * mm, v(38.47, 33.14) * mm, v(40.77, 32.1) * mm, v(42.56, 31.41) * mm, v(45.19, 30.53) * mm, v(46.52, 29.93) * mm, v(46.8, 30.17) * mm, v(46.3, 31.93) * mm, v(46, 33.9) * mm, v(45.22, 35.68) * mm, v(46.16, 34.74) * mm, v(46.64, 32.5) * mm, v(47.1, 30.8) * mm, v(47.46, 29.78) * mm, v(49.3, 28.84) * mm, v(51, 28.3) * mm, v(51.57, 29.02) * mm, v(51.42, 31.08) * mm, v(51.7, 33.14) * mm, v(51.84, 34.25) * mm, v(51.87, 32.02) * mm, v(51.93, 30.44) * mm, v(51.87, 28.08) * mm, v(52.84, 27.63) * mm, v(54.47, 27.12) * mm, v(55.2, 26.78) * mm, v(55.62, 28.33) * mm, v(56.23, 31.17) * mm, v(56.56, 34.38) * mm, v(56.74, 35.68) * mm, v(56.9, 34.13) * mm, v(56.68, 32.02) * mm, v(56.23, 29.08) * mm, v(55.68, 27.2) * mm, v(55.86, 26.6) * mm, v(57.44, 26.15) * mm, v(58.2, 25.94) * mm, v(57.69, 25.18) * mm]});
            skFitSpline(sketch, "E32", {"points": [v(44.92, 33.92) * mm, v(44.61, 32.77) * mm, v(45.11, 31.64) * mm, v(45.76, 31.24) * mm, v(45.87, 32.41) * mm, v(45.46, 33.53) * mm, v(44.92, 33.92) * mm]});
            skFitSpline(sketch, "E33", {"points": [v(50.09, 32.62) * mm, v(49.8, 31.72) * mm, v(49.94, 30.62) * mm, v(50.27, 29.74) * mm, v(50.59, 29.38) * mm, v(50.88, 29.86) * mm, v(50.77, 31.52) * mm, v(50.09, 32.62) * mm]});
            skFitSpline(sketch, "E34", {"points": [v(54.89, 29.78) * mm, v(54.58, 30.23) * mm, v(53.97, 29.17) * mm, v(54.33, 28.25) * mm, v(54.58, 29.06) * mm, v(54.89, 29.78) * mm]});
            skFitSpline(sketch, "E35", {"points": [v(76.94, 28.33) * mm, v(77.68, 29.82) * mm, v(77.51, 32.13) * mm, v(78.55, 35.64) * mm, v(79.41, 37.42) * mm, v(78.66, 38.17) * mm, v(77.34, 40.53) * mm, v(76.94, 42.03) * mm, v(76.88, 42.84) * mm, v(78.03, 41.8) * mm, v(78.55, 39.9) * mm, v(79.35, 38.52) * mm, v(80.28, 39.61) * mm, v(81.08, 41.57) * mm, v(81.54, 42.72) * mm, v(80.8, 43.13) * mm, v(79.47, 45.08) * mm, v(79.53, 49.23) * mm, v(79.81, 51.13) * mm, v(80.28, 53.6) * mm, v(80.62, 53.95) * mm, v(80.8, 52.28) * mm, v(80.16, 48.42) * mm, v(80.22, 45.49) * mm, v(81.2, 43.82) * mm, v(81.83, 43.59) * mm, v(82.75, 45.95) * mm, v(83.96, 48.37) * mm, v(83.53, 48.95) * mm, v(83.53, 52) * mm, v(84.45, 55.63) * mm, v(85.83, 58.22) * mm, v(86.64, 59.95) * mm, v(86.81, 61.33) * mm, v(87.33, 61.5) * mm, v(87.33, 59.95) * mm, v(86, 57.07) * mm, v(84.74, 54.54) * mm, v(83.99, 51.14) * mm, v(84.1, 49.24) * mm, v(86.52, 52.35) * mm, v(89.4, 54.65) * mm, v(90.96, 55.63) * mm, v(92.62, 58.4) * mm, v(92.42, 61.96) * mm, v(92.28, 64.97) * mm, v(92.49, 65.59) * mm, v(92.97, 65.66) * mm, v(93.24, 63.6) * mm, v(93.51, 60.25) * mm, v(92.56, 56.41) * mm, v(95.3, 57.85) * mm, v(96.53, 58.67) * mm, v(98.03, 61.9) * mm, v(97.97, 64.29) * mm, v(97.28, 66.34) * mm, v(96.87, 68.12) * mm, v(96.87, 68.74) * mm, v(97.55, 68.46) * mm, v(97.97, 66.2) * mm, v(98.79, 63.4) * mm, v(98.51, 61) * mm, v(97.76, 58.88) * mm, v(99.06, 60.1) * mm, v(101.12, 61.75) * mm, v(101.87, 62.64) * mm, v(101.46, 64.77) * mm, v(100.84, 68.05) * mm, v(100.7, 70.18) * mm, v(100.84, 71.68) * mm, v(101.32, 71.48) * mm, v(101.25, 69.5) * mm, v(101.73, 66.62) * mm, v(102.21, 63.88) * mm, v(102.62, 63.26) * mm, v(104.4, 65.59) * mm, v(105.43, 67.03) * mm, v(104.75, 67.99) * mm, v(104.2, 70.31) * mm, v(103.86, 72.1) * mm, v(104.06, 74.15) * mm, v(104.47, 74.35) * mm, v(104.47, 72.37) * mm, v(104.95, 69.63) * mm, v(105.77, 67.64) * mm, v(108, 70.9) * mm, v(109.4, 73) * mm, v(110.27, 74.54) * mm, v(110.54, 75.13) * mm, v(111.11, 74.8) * mm, v(110.34, 73.5) * mm, v(108.7, 70.2) * mm, v(106.63, 67.36) * mm, v(107.81, 67.85) * mm, v(109.48, 69.1) * mm, v(110.99, 70.86) * mm, v(111.31, 71.55) * mm, v(111.8, 71.3) * mm, v(110.87, 69.56) * mm, v(109.28, 67.89) * mm, v(107.04, 66.79) * mm, v(106.3, 66.5) * mm, v(105.04, 65.28) * mm, v(103.9, 63.73) * mm, v(106.27, 64.16) * mm, v(107.84, 64.91) * mm, v(109.42, 65.6) * mm, v(109.62, 64.91) * mm, v(107.98, 64.16) * mm, v(105.48, 63.31) * mm, v(103.4, 63.31) * mm, v(102.37, 61.81) * mm, v(100.47, 60.26) * mm, v(101.56, 60.2) * mm, v(104.44, 60.95) * mm, v(105.65, 61.7) * mm, v(106.06, 62.22) * mm, v(106.46, 61.99) * mm, v(105.7, 60.78) * mm, v(103.7, 60.03) * mm, v(101.5, 59.63) * mm, v(99.6, 59.28) * mm, v(98.1, 58.3) * mm, v(95.8, 57.03) * mm, v(93.62, 55.94) * mm, v(94.02, 55.65) * mm, v(97.53, 55.77) * mm, v(100.53, 56.34) * mm, v(103.52, 57.61) * mm, v(103.85, 57.37) * mm, v(103.96, 57.1) * mm, v(103.72, 56.77) * mm, v(102.59, 56.2) * mm, v(100.9, 55.63) * mm, v(98.77, 55.11) * mm, v(96.34, 54.9) * mm, v(94.6, 54.94) * mm, v(93.27, 55.03) * mm, v(91.92, 55.03) * mm, v(90.73, 54.74) * mm, v(89.47, 53.85) * mm, v(87.75, 52.52) * mm, v(86.66, 51.32) * mm, v(85.6, 49.88) * mm, v(84.98, 48.68) * mm, v(85.97, 49.44) * mm, v(87.72, 49.98) * mm, v(89.84, 50.67) * mm, v(91.45, 50.6) * mm, v(93.44, 50.7) * mm, v(95.63, 50.8) * mm, v(96.7, 51.18) * mm, v(97.89, 51.8) * mm, v(98.03, 51.94) * mm, v(98.4, 51.7) * mm, v(97.72, 51.08) * mm, v(96.38, 50.36) * mm, v(94.12, 50.12) * mm, v(91.9, 50.12) * mm, v(90.22, 50.02) * mm, v(88.3, 49.7) * mm, v(86.35, 48.92) * mm, v(84.95, 47.96) * mm, v(84.26, 47.38) * mm, v(83.65, 46.25) * mm, v(83.2, 45.19) * mm, v(84.33, 45.3) * mm, v(86.97, 46.35) * mm, v(88.92, 46.7) * mm, v(90.87, 47.18) * mm, v(93.4, 47.38) * mm, v(95.87, 47.28) * mm, v(95.87, 46.94) * mm, v(94.43, 46.94) * mm, v(93.06, 46.73) * mm, v(90.19, 46.42) * mm, v(87.51, 45.8) * mm, v(85.36, 45.02) * mm, v(83.23, 44.33) * mm, v(82.72, 43.92) * mm, v(81.98, 42.03) * mm, v(80.82, 39.46) * mm, v(80.29, 38.15) * mm, v(81.45, 38.88) * mm, v(83.29, 40.77) * mm, v(85.32, 41.88) * mm, v(87.84, 41.93) * mm, v(90.36, 41.83) * mm, v(91.23, 41.88) * mm, v(91.28, 41.3) * mm, v(89.15, 41.45) * mm, v(86.39, 41.2) * mm, v(83.68, 40.09) * mm, v(81.64, 38.44) * mm, v(80.43, 37.09) * mm, v(79.75, 36.4) * mm, v(78.98, 34.76) * mm, v(78.54, 33.02) * mm, v(78.3, 31.42) * mm, v(78.93, 31.76) * mm, v(80.19, 33.8) * mm, v(82.76, 35.49) * mm, v(85.95, 36.8) * mm, v(87.26, 36.94) * mm, v(87.11, 36.31) * mm, v(85.61, 36.07) * mm, v(82.9, 34.86) * mm, v(80.58, 33.16) * mm, v(79.32, 31.18) * mm, v(78.74, 29.92) * mm, v(77.96, 28.42) * mm, v(77.28, 27.7) * mm, v(76.94, 28.33) * mm]});
            skFitSpline(sketch, "E36", {"points": [v(118.79, 17.09) * mm, v(119.13, 17.95) * mm, v(118.69, 18.32) * mm, v(118.2, 18.5) * mm, v(118.07, 19.31) * mm, v(118.62, 20.48) * mm, v(118.34, 20.82) * mm, v(117.87, 19.62) * mm, v(117.6, 19.14) * mm, v(116.08, 19.49) * mm, v(114.61, 20.3) * mm, v(112.7, 21.34) * mm, v(111.22, 22.05) * mm, v(111.43, 22.77) * mm, v(112.79, 25.3) * mm, v(113.08, 27.31) * mm, v(112.94, 28.75) * mm, v(112.84, 28.01) * mm, v(112.72, 27.07) * mm, v(112.36, 25.82) * mm, v(111.65, 24.3) * mm, v(110.82, 23.29) * mm, v(110.3, 22.84) * mm, v(107.33, 24.28) * mm, v(106.12, 25.06) * mm, v(105.12, 25.52) * mm, v(104.93, 26.56) * mm, v(105.25, 27.74) * mm, v(105.3, 29.15) * mm, v(105.1, 30.24) * mm, v(104.88, 31.18) * mm, v(104.93, 29.83) * mm, v(104.93, 28.57) * mm, v(104.52, 27.19) * mm, v(104.03, 26.1) * mm, v(102.52, 26.98) * mm, v(100.77, 27.92) * mm, v(99.14, 28.81) * mm, v(98.66, 29.46) * mm, v(98.74, 31.42) * mm, v(98.5, 32.76) * mm, v(97.8, 34.02) * mm, v(98.25, 32.68) * mm, v(98.25, 31.3) * mm, v(97.96, 29.95) * mm, v(95.38, 31) * mm, v(93.53, 32) * mm, v(92.33, 32.6) * mm, v(92.78, 32.06) * mm, v(94.25, 31.1) * mm, v(96.1, 30.1) * mm, v(97.3, 29.4) * mm, v(97.42, 28.85) * mm, v(96.53, 27.75) * mm, v(95.5, 27.14) * mm, v(93.92, 26.81) * mm, v(95.06, 26.6) * mm, v(96.57, 27.18) * mm, v(97.5, 28.24) * mm, v(98.4, 28.8) * mm, v(99.62, 28.11) * mm, v(100.72, 27.38) * mm, v(102.27, 26.57) * mm, v(103.37, 25.83) * mm, v(103.86, 25.75) * mm, v(103.28, 25.06) * mm, v(102.35, 24.04) * mm, v(101.05, 23.43) * mm, v(99.82, 22.86) * mm, v(101.17, 23.15) * mm, v(102.63, 23.76) * mm, v(103.61, 24.74) * mm, v(104.34, 25.39) * mm, v(105.73, 24.57) * mm, v(107.23, 23.84) * mm, v(108.17, 23.27) * mm, v(109.43, 22.78) * mm, v(110.19, 22.3) * mm, v(110.2, 21.54) * mm, v(109.52, 20.43) * mm, v(108.5, 19.35) * mm, v(107.35, 18.74) * mm, v(107.77, 18.6) * mm, v(109.04, 19.35) * mm, v(109.91, 20.28) * mm, v(110.56, 21.18) * mm, v(110.79, 21.65) * mm, v(111.28, 21.5) * mm, v(111.88, 21.2) * mm, v(112.74, 20.74) * mm, v(113.58, 20.26) * mm, v(114.62, 19.6) * mm, v(115.89, 18.77) * mm, v(116.8, 18.28) * mm, v(116.91, 17.39) * mm, v(115.85, 16.26) * mm, v(115.03, 15.54) * mm, v(115.71, 15.64) * mm, v(116.5, 16.19) * mm, v(117.08, 17.15) * mm, v(117.46, 17.73) * mm, v(118.08, 17.42) * mm, v(118.79, 17.09) * mm]});
            skFitSpline(sketch, "E37", {"points": [v(134.02, 23.6) * mm, v(136.87, 24.33) * mm, v(137.36, 25.4) * mm, v(136.99, 26.28) * mm, v(136.65, 28.23) * mm, v(136.54, 30.08) * mm, v(136.68, 32.86) * mm, v(136.78, 34.84) * mm, v(137.13, 36.62) * mm, v(137.3, 35.22) * mm, v(137.06, 32.79) * mm, v(137.02, 30.32) * mm, v(137.16, 27.92) * mm, v(137.7, 25.8) * mm, v(138.19, 25.25) * mm, v(140.35, 26.21) * mm, v(141.3, 26.66) * mm, v(141.17, 28.92) * mm, v(141.58, 31.52) * mm, v(142.33, 34.4) * mm, v(143.87, 37.17) * mm, v(144.35, 37.75) * mm, v(142.54, 33.71) * mm, v(141.78, 30.83) * mm, v(141.85, 27.14) * mm, v(143.63, 27.55) * mm, v(145.82, 28.44) * mm, v(146.61, 28.88) * mm, v(147.2, 30.13) * mm, v(147.34, 31.31) * mm, v(147.8, 32.43) * mm, v(148.46, 33.49) * mm, v(147.83, 31.66) * mm, v(147.44, 29.9) * mm, v(147.36, 28.95) * mm, v(148.4, 29.36) * mm, v(150.43, 30.27) * mm, v(155.83, 31.78) * mm, v(159.26, 32.8) * mm, v(156.08, 31.3) * mm, v(153.5, 30.35) * mm, v(151.11, 29.58) * mm, v(149.7, 28.98) * mm, v(147.8, 28.24) * mm, v(145.97, 27.63) * mm, v(145.83, 27.18) * mm, v(146.41, 26.75) * mm, v(147.1, 26.27) * mm, v(147.94, 25.66) * mm, v(149.04, 24.84) * mm, v(149.88, 24.52) * mm, v(150.72, 23.92) * mm, v(149.9, 24.18) * mm, v(149.03, 24.55) * mm, v(147.8, 25.25) * mm, v(146.72, 26) * mm, v(145.62, 26.91) * mm, v(145.35, 27.15) * mm, v(143.32, 26.56) * mm, v(142, 26) * mm, v(141.13, 25.73) * mm, v(141.42, 25.25) * mm, v(141.95, 24.53) * mm, v(142.38, 24.06) * mm, v(142.75, 23.6) * mm, v(143.34, 23.02) * mm, v(143.83, 22.43) * mm, v(144.38, 21.8) * mm, v(144.1, 21.82) * mm, v(143.44, 22.64) * mm, v(142.47, 23.68) * mm, v(141.84, 24.35) * mm, v(141.35, 24.92) * mm, v(140.92, 25.36) * mm, v(139.69, 25.05) * mm, v(138.55, 24.61) * mm, v(137.73, 24.25) * mm, v(137.6, 24.08) * mm, v(137.92, 23.43) * mm, v(138.36, 22.34) * mm, v(139.06, 21.44) * mm, v(139.64, 20.33) * mm, v(140.51, 19.29) * mm, v(141.4, 18.05) * mm, v(140.83, 18.46) * mm, v(139.95, 19.46) * mm, v(139.35, 20.38) * mm, v(138.72, 21.2) * mm, v(138.16, 22.1) * mm, v(137.63, 23.11) * mm, v(137.34, 23.91) * mm, v(136.37, 23.64) * mm, v(135.2, 23.09) * mm, v(134.55, 22.65) * mm, v(134.02, 23.6) * mm]});
            skFitSpline(sketch, "E38", {"points": [v(142.96, 30.6) * mm, v(142.61, 29.42) * mm, v(142.47, 28.47) * mm, v(143.04, 28.67) * mm, v(143.42, 29.83) * mm, v(143.45, 30.63) * mm, v(142.96, 30.6) * mm]});
            skFitSpline(sketch, "E39", {"points": [v(150.36, 33.8) * mm, v(149.72, 33.08) * mm, v(148.86, 31.4) * mm, v(148.48, 30.4) * mm, v(148.77, 30.26) * mm, v(149.66, 30.72) * mm, v(150.3, 32.42) * mm, v(150.36, 33.8) * mm]});
            skFitSpline(sketch, "E40", {"points": [v(149.09, 26.7) * mm, v(148.4, 27.11) * mm, v(147.2, 27.14) * mm, v(147.57, 26.6) * mm, v(148.37, 25.85) * mm, v(149.06, 25.53) * mm, v(149.52, 25.9) * mm, v(149.09, 26.7) * mm]});
            skFitSpline(sketch, "E41", {"points": [v(143.51, 25.17) * mm, v(142.88, 25.27) * mm, v(142.6, 24.82) * mm, v(143.2, 24.26) * mm, v(144.38, 23.33) * mm, v(145.05, 23.5) * mm, v(144.5, 24.22) * mm, v(143.51, 25.17) * mm]});
            skFitSpline(sketch, "E42", {"points": [v(139.71, 23.53) * mm, v(139.16, 23.59) * mm, v(139.4, 23.02) * mm, v(139.82, 22.14) * mm, v(140.2, 22.02) * mm, v(140.2, 22.55) * mm, v(140.02, 23.1) * mm, v(139.71, 23.53) * mm]});
            skFitSpline(sketch, "E43", {"points": [v(128.96, 36.43) * mm, v(127.81, 34.93) * mm, v(127.4, 34.59) * mm, v(128.27, 33.1) * mm, v(129.54, 31.6) * mm, v(129.83, 32.51) * mm, v(130.06, 33.95) * mm, v(129.71, 35.1) * mm, v(128.96, 36.43) * mm]});
            skFitSpline(sketch, "E44", {"points": [v(136.5, 55.19) * mm, v(133.73, 54.53) * mm, v(132.35, 53.56) * mm, v(132.5, 49.97) * mm, v(132.92, 47.94) * mm, v(134.06, 50.54) * mm, v(135.52, 52.42) * mm, v(136.9, 54.37) * mm, v(136.5, 55.19) * mm]});
            skSolve(sketch);
        }
        {
            var Q0;
            Q0=makeQuery(id+"F6.imprint","IMPRINT",FACE,{"disambiguationData":[TD([[makeQuery(id+"F6.imprint","IMPRINT",EDGE,{"derivedFrom":sQuery(id+"F6.wireOp",EDGE,"E24")}),-1.0]])]});
            var Q1;
            Q1=makeQuery(id+"F6.imprint","IMPRINT",FACE,{"disambiguationData":[TD([[makeQuery(id+"F6.imprint","IMPRINT",EDGE,{"derivedFrom":sQuery(id+"F6.wireOp",EDGE,"E26")}),1.0]])]});
            var Q2;
            Q2=makeQuery(id+"F6.imprint","IMPRINT",FACE,{"disambiguationData":[TD([[makeQuery(id+"F6.imprint","IMPRINT",EDGE,{"derivedFrom":sQuery(id+"F6.wireOp",EDGE,"E27")}),1.0]])]});
            var Q3;
            Q3=makeQuery(id+"F6.imprint","IMPRINT",FACE,{"disambiguationData":[TD([[makeQuery(id+"F6.imprint","IMPRINT",EDGE,{"derivedFrom":sQuery(id+"F6.wireOp",EDGE,"E31")}),-1.0]])]});
            var Q4;
            Q4=makeQuery(id+"F6.imprint","IMPRINT",FACE,{"disambiguationData":[TD([[makeQuery(id+"F6.imprint","IMPRINT",EDGE,{"derivedFrom":sQuery(id+"F6.wireOp",EDGE,"E32")}),1.0]])]});
            var Q5;
            Q5=makeQuery(id+"F6.imprint","IMPRINT",FACE,{"disambiguationData":[TD([[makeQuery(id+"F6.imprint","IMPRINT",EDGE,{"derivedFrom":sQuery(id+"F6.wireOp",EDGE,"E28")}),1.0]])]});
            var Q6;
            Q6=makeQuery(id+"F6.imprint","IMPRINT",FACE,{"disambiguationData":[TD([[makeQuery(id+"F6.imprint","IMPRINT",EDGE,{"derivedFrom":sQuery(id+"F6.wireOp",EDGE,"E33")}),1.0]])]});
            var Q7;
            Q7=makeQuery(id+"F6.imprint","IMPRINT",FACE,{"disambiguationData":[TD([[makeQuery(id+"F6.imprint","IMPRINT",EDGE,{"derivedFrom":sQuery(id+"F6.wireOp",EDGE,"E34")}),1.0]])]});
            var Q8;
            Q8=makeQuery(id+"F6.imprint","IMPRINT",FACE,{"disambiguationData":[TD([[makeQuery(id+"F6.imprint","IMPRINT",EDGE,{"derivedFrom":sQuery(id+"F6.wireOp",EDGE,"E30")}),1.0]])]});
            var Q9;
            Q9=makeQuery(id+"F6.imprint","IMPRINT",FACE,{"disambiguationData":[TD([[makeQuery(id+"F6.imprint","IMPRINT",EDGE,{"derivedFrom":sQuery(id+"F6.wireOp",EDGE,"E29")}),1.0]])]});
            var Q10;
            Q10=makeQuery(id+"F6.imprint","IMPRINT",FACE,{"disambiguationData":[TD([[makeQuery(id+"F6.imprint","IMPRINT",EDGE,{"derivedFrom":sQuery(id+"F6.wireOp",EDGE,"E35")}),-1.0]])]});
            var Q11;
            Q11=makeQuery(id+"F6.imprint","IMPRINT",FACE,{"disambiguationData":[TD([[makeQuery(id+"F6.imprint","IMPRINT",EDGE,{"derivedFrom":sQuery(id+"F6.wireOp",EDGE,"E36")}),1.0]])]});
            var Q12;
            Q12=makeQuery(id+"F6.imprint","IMPRINT",FACE,{"disambiguationData":[TD([[makeQuery(id+"F6.imprint","IMPRINT",EDGE,{"derivedFrom":sQuery(id+"F6.wireOp",EDGE,"E44")}),1.0]])]});
            var Q13;
            Q13=makeQuery(id+"F6.imprint","IMPRINT",FACE,{"disambiguationData":[TD([[makeQuery(id+"F6.imprint","IMPRINT",EDGE,{"derivedFrom":sQuery(id+"F6.wireOp",EDGE,"E43")}),1.0]])]});
            var Q14;
            Q14=makeQuery(id+"F6.imprint","IMPRINT",FACE,{"disambiguationData":[TD([[makeQuery(id+"F6.imprint","IMPRINT",EDGE,{"derivedFrom":sQuery(id+"F6.wireOp",EDGE,"E37")}),-1.0]])]});
            var Q15;
            Q15=makeQuery(id+"F6.imprint","IMPRINT",FACE,{"disambiguationData":[TD([[makeQuery(id+"F6.imprint","IMPRINT",EDGE,{"derivedFrom":sQuery(id+"F6.wireOp",EDGE,"E42")}),1.0]])]});
            var Q16;
            Q16=makeQuery(id+"F6.imprint","IMPRINT",FACE,{"disambiguationData":[TD([[makeQuery(id+"F6.imprint","IMPRINT",EDGE,{"derivedFrom":sQuery(id+"F6.wireOp",EDGE,"E41")}),1.0]])]});
            var Q17;
            Q17=makeQuery(id+"F6.imprint","IMPRINT",FACE,{"disambiguationData":[TD([[makeQuery(id+"F6.imprint","IMPRINT",EDGE,{"derivedFrom":sQuery(id+"F6.wireOp",EDGE,"E38")}),1.0]])]});
            var Q18;
            Q18=makeQuery(id+"F6.imprint","IMPRINT",FACE,{"disambiguationData":[TD([[makeQuery(id+"F6.imprint","IMPRINT",EDGE,{"derivedFrom":sQuery(id+"F6.wireOp",EDGE,"E40")}),1.0]])]});
            var Q19;
            Q19=makeQuery(id+"F6.imprint","IMPRINT",FACE,{"disambiguationData":[TD([[makeQuery(id+"F6.imprint","IMPRINT",EDGE,{"derivedFrom":sQuery(id+"F6.wireOp",EDGE,"E39")}),1.0]])]});
            var Q20;
            Q20=makeQuery(id+"F6.imprint","IMPRINT",FACE,{"disambiguationData":[TD([[makeQuery(id+"F6.imprint","IMPRINT",EDGE,{"derivedFrom":sQuery(id+"F6.wireOp",EDGE,"E25")}),1.0]])]});
            extrude(context, id + "F7", {"entities" : qUnion([Q0, Q1, Q2, Q3, Q4, Q5, Q6, Q7, Q8, Q9, Q10, Q11, Q12, Q13, Q14, Q15, Q16, Q17, Q18, Q19, Q20]), "operationType" : NewBodyOperationType.REMOVE, "oppositeDirection" : true, "depth" : 2 * mm, "offsetDistance" : 25 * mm});
        }
    });
